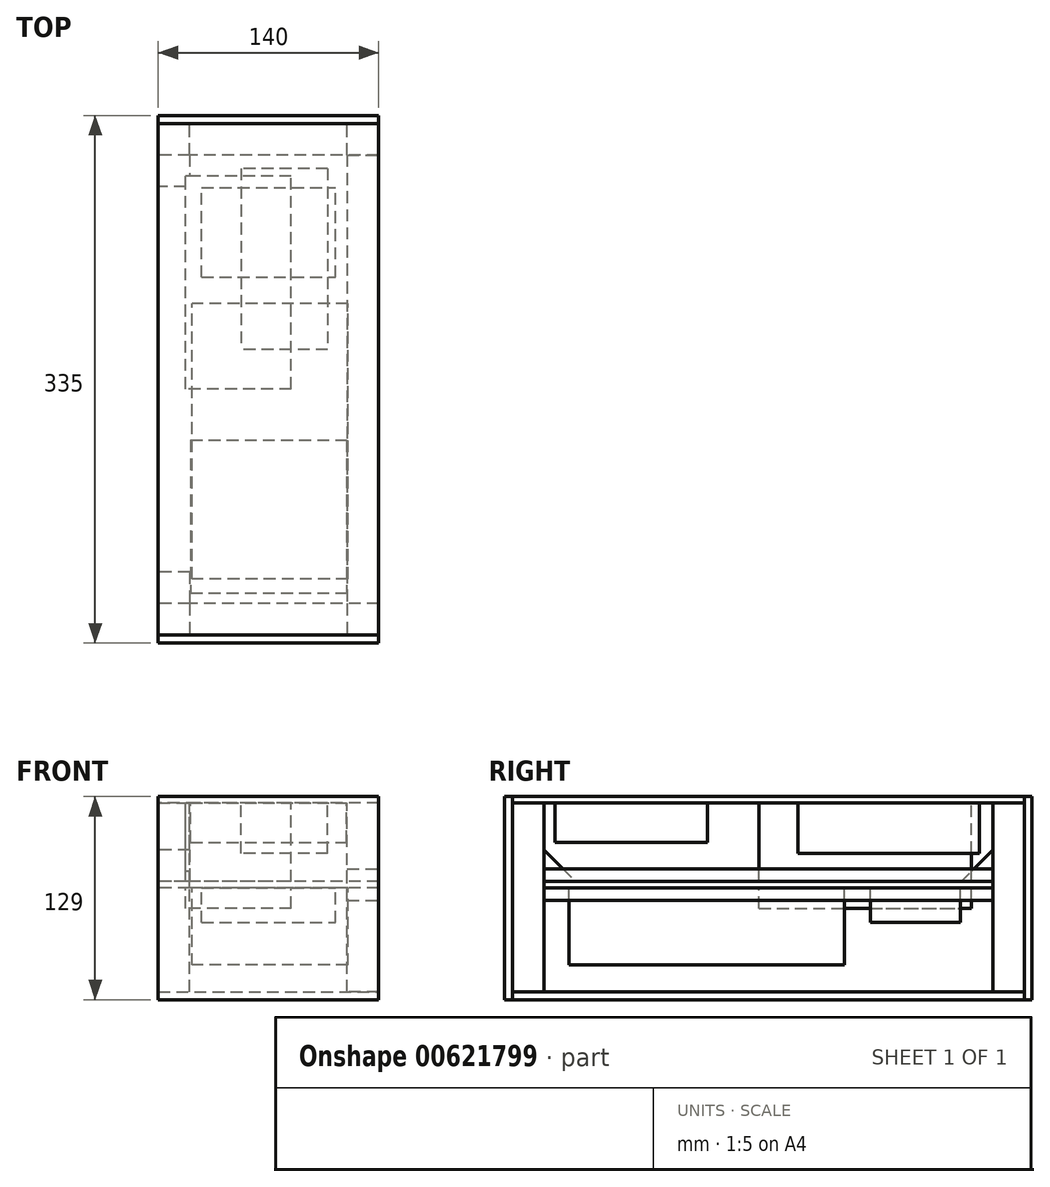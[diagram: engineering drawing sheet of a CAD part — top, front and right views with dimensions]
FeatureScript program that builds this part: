
annotation { "Feature Type Name" : "Feature", "Feature Type Description" : "" }
export const myFeature = defineFeature(function(context is Context, id is Id, definition is map)
    precondition{}
    {
        {
            var Q0;
            Q0=qCreatedBy(makeId("Top.planeOp"),FACE);
            var sketch = newSketch(context, id + "F0", { "sketchPlane" : qUnion([Q0])});
            skLineSegment(sketch, "E0.bottom", {"start": v(70, 142.5) * mm, "end": v(-70, 142.5) * mm, "construction": true});
            skLineSegment(sketch, "E0.top", {"start": v(70, -142.5) * mm, "end": v(-70, -142.5) * mm, "construction": true});
            skLineSegment(sketch, "E0.left", {"start": v(70, 142.5) * mm, "end": v(70, -142.5) * mm, "construction": true});
            skLineSegment(sketch, "E0.right", {"start": v(-70, 142.5) * mm, "end": v(-70, -142.5) * mm, "construction": true});
            skPoint(sketch, "E0.middle", {"position": v(0, 0) * mm});
            skLineSegment(sketch, "E1.bottom", {"start": v(70, -142.5) * mm, "end": v(50, -142.5) * mm});
            skLineSegment(sketch, "E1.top", {"start": v(70, -162.5) * mm, "end": v(50, -162.5) * mm});
            skLineSegment(sketch, "E1.left", {"start": v(70, -142.5) * mm, "end": v(70, -162.5) * mm});
            skLineSegment(sketch, "E1.right", {"start": v(50, -142.5) * mm, "end": v(50, -162.5) * mm});
            skLineSegment(sketch, "E2.bottom", {"start": v(-70, -142.5) * mm, "end": v(-50, -142.5) * mm});
            skLineSegment(sketch, "E2.top", {"start": v(-70, -162.5) * mm, "end": v(-50, -162.5) * mm});
            skLineSegment(sketch, "E2.left", {"start": v(-70, -142.5) * mm, "end": v(-70, -162.5) * mm});
            skLineSegment(sketch, "E2.right", {"start": v(-50, -142.5) * mm, "end": v(-50, -162.5) * mm});
            skLineSegment(sketch, "E3.bottom", {"start": v(-70, 142.5) * mm, "end": v(-50, 142.5) * mm});
            skLineSegment(sketch, "E3.top", {"start": v(-70, 162.5) * mm, "end": v(-50, 162.5) * mm});
            skLineSegment(sketch, "E3.left", {"start": v(-70, 142.5) * mm, "end": v(-70, 162.5) * mm});
            skLineSegment(sketch, "E3.right", {"start": v(-50, 142.5) * mm, "end": v(-50, 162.5) * mm});
            skLineSegment(sketch, "E4.bottom", {"start": v(70, 142.5) * mm, "end": v(50, 142.5) * mm});
            skLineSegment(sketch, "E4.top", {"start": v(70, 162.5) * mm, "end": v(50, 162.5) * mm});
            skLineSegment(sketch, "E4.left", {"start": v(70, 142.5) * mm, "end": v(70, 162.5) * mm});
            skLineSegment(sketch, "E4.right", {"start": v(50, 142.5) * mm, "end": v(50, 162.5) * mm});
            skSolve(sketch);
        }
        {
            var Q0;
            Q0=qCreatedBy(makeId("Top.planeOp"),FACE);
            var sketch = newSketch(context, id + "F1", { "sketchPlane" : qUnion([Q0])});
            skLineSegment(sketch, "E5.bottom", {"start": v(70, -162.5) * mm, "end": v(-70, -162.5) * mm});
            skLineSegment(sketch, "E5.top", {"start": v(70, 162.5) * mm, "end": v(-70, 162.5) * mm});
            skLineSegment(sketch, "E5.left", {"start": v(70, -162.5) * mm, "end": v(70, 162.5) * mm});
            skLineSegment(sketch, "E5.right", {"start": v(-70, -162.5) * mm, "end": v(-70, 162.5) * mm});
            skSolve(sketch);
        }
        {
            var Q0;
            Q0 = qSketchRegion(id + "F1", true);
            extrude(context, id + "F2", {"entities" : qUnion([Q0]), "depth" : 4 * mm, "offsetDistance" : 25 * mm});
        }
        {
            var Q0;
            Q0 = qSketchRegion(id + "F0", true);
            extrude(context, id + "F3", {"entities" : qUnion([Q0]), "oppositeDirection" : true, "depth" : 120 * mm, "offsetDistance" : 25 * mm});
        }
        {
            var Q0;
            Q0=qCreatedBy(makeId("Top.planeOp"),FACE);
            cPlane(context, id + "F4", {"entities" : qUnion([Q0]), "cplaneType" : CPlaneType.OFFSET, "offset" : 50 * mm, "oppositeDirection" : true, "width" : 150 * mm, "height" : 150 * mm});
        }
        {
            var Q0;
            Q0=qCreatedBy(id+"F4.planeOp",FACE);
            var sketch = newSketch(context, id + "F5", { "sketchPlane" : qUnion([Q0])});
            skLineSegment(sketch, "E6.bottom", {"start": v(50, -162.5) * mm, "end": v(-50, -162.5) * mm, "construction": true});
            skLineSegment(sketch, "E6.top", {"start": v(50, 162.5) * mm, "end": v(-50, 162.5) * mm, "construction": true});
            skLineSegment(sketch, "E6.left", {"start": v(70, -142.5) * mm, "end": v(70, 142.5) * mm});
            skLineSegment(sketch, "E6.right", {"start": v(-70, -142.5) * mm, "end": v(-70, 142.5) * mm});
            skLineSegment(sketch, "E7.0", {"start": v(70, -142.5) * mm, "end": v(50, -142.5) * mm});
            skLineSegment(sketch, "E7.1", {"start": v(50, -142.5) * mm, "end": v(50, -162.5) * mm, "construction": true});
            skLineSegment(sketch, "E7.2", {"start": v(-50, -142.5) * mm, "end": v(-50, -162.5) * mm, "construction": true});
            skLineSegment(sketch, "E7.3", {"start": v(-70, -142.5) * mm, "end": v(-50, -142.5) * mm});
            skLineSegment(sketch, "E7.4", {"start": v(-70, 142.5) * mm, "end": v(-50, 142.5) * mm});
            skLineSegment(sketch, "E7.5", {"start": v(-50, 142.5) * mm, "end": v(-50, 162.5) * mm, "construction": true});
            skLineSegment(sketch, "E7.6", {"start": v(50, 142.5) * mm, "end": v(50, 162.5) * mm, "construction": true});
            skLineSegment(sketch, "E7.7", {"start": v(70, 142.5) * mm, "end": v(50, 142.5) * mm});
            skLineSegment(sketch, "E8", {"start": v(50, -142.5) * mm, "end": v(-50, -142.5) * mm});
            skLineSegment(sketch, "E9", {"start": v(50, 142.5) * mm, "end": v(-50, 142.5) * mm});
            skSolve(sketch);
        }
        {
            var Q0;
            Q0 = qSketchRegion(id + "F5", true);
            extrude(context, id + "F6", {"entities" : qUnion([Q0]), "oppositeDirection" : true, "depth" : 4 * mm, "offsetDistance" : 25 * mm});
        }
        {
            var Q0;
            Q0=makeQuery(id+"F2.opExtrude","CAP_FACE",FACE,{"disambiguationData":[OSD([sQuery(id+"F1.wireOp",EDGE,"E5.bottom"),sQuery(id+"F1.wireOp",EDGE,"E5.top"),sQuery(id+"F1.wireOp",EDGE,"E5.left"),sQuery(id+"F1.wireOp",EDGE,"E5.right")])],"isStart":true});
            var sketch = newSketch(context, id + "F7", { "sketchPlane" : qUnion([Q0])});
            skLineSegment(sketch, "E10.bottom", {"start": v(37.67, -133.95) * mm, "end": v(-17.33, -133.95) * mm});
            skLineSegment(sketch, "E10.top", {"start": v(37.67, -18.95) * mm, "end": v(-17.33, -18.95) * mm});
            skLineSegment(sketch, "E10.left", {"start": v(37.67, -133.95) * mm, "end": v(37.67, -18.95) * mm});
            skLineSegment(sketch, "E10.right", {"start": v(-17.33, -133.95) * mm, "end": v(-17.33, -18.95) * mm});
            skPoint(sketch, "E10.middle", {"position": v(10.17, -76.45) * mm});
            skSolve(sketch);
        }
        {
            var Q0;
            Q0 = qSketchRegion(id + "F7", true);
            extrude(context, id + "F8", {"entities" : qUnion([Q0]), "depth" : 32 * mm, "offsetDistance" : 25 * mm});
        }
        {
            var Q0;
            Q0=makeQuery(id+"F6.opExtrude","CAP_FACE",FACE,{"disambiguationData":[OSD([sQuery(id+"F5.wireOp",EDGE,"E6.bottom"),sQuery(id+"F5.wireOp",EDGE,"E6.top"),sQuery(id+"F5.wireOp",EDGE,"E6.left"),sQuery(id+"F5.wireOp",EDGE,"E6.right"),sQuery(id+"F5.wireOp",EDGE,"E7.0"),sQuery(id+"F5.wireOp",EDGE,"E7.1"),sQuery(id+"F5.wireOp",EDGE,"E7.2"),sQuery(id+"F5.wireOp",EDGE,"E7.3"),sQuery(id+"F5.wireOp",EDGE,"E7.4"),sQuery(id+"F5.wireOp",EDGE,"E7.5"),sQuery(id+"F5.wireOp",EDGE,"E7.6"),sQuery(id+"F5.wireOp",EDGE,"E7.7")])],"isStart":false});
            var sketch = newSketch(context, id + "F9", { "sketchPlane" : qUnion([Q0])});
            skLineSegment(sketch, "E11.bottom", {"start": v(50.48, 126.75) * mm, "end": v(-48.52, 126.75) * mm});
            skLineSegment(sketch, "E11.top", {"start": v(50.48, -48.25) * mm, "end": v(-48.52, -48.25) * mm});
            skLineSegment(sketch, "E11.left", {"start": v(50.48, 126.75) * mm, "end": v(50.48, -48.25) * mm});
            skLineSegment(sketch, "E11.right", {"start": v(-48.52, 126.75) * mm, "end": v(-48.52, -48.25) * mm});
            skPoint(sketch, "E12.startSnap0", {"position": v(70, 0) * mm});
            skSolve(sketch);
        }
        {
            var Q0;
            Q0 = qSketchRegion(id + "F9", true);
            extrude(context, id + "F10", {"entities" : qUnion([Q0]), "depth" : 49 * mm, "offsetDistance" : 25 * mm});
        }
        {
            var Q0;
            Q0=qCreatedBy(id+"F4.planeOp",FACE);
            cPlane(context, id + "F11", {"entities" : qUnion([Q0]), "cplaneType" : CPlaneType.OFFSET, "offset" : 75 * mm, "oppositeDirection" : true, "width" : 150 * mm, "height" : 150 * mm});
        }
        {
            var Q0;
            Q0=makeQuery(id+"F2.opExtrude","CAP_FACE",FACE,{"disambiguationData":[OSD([sQuery(id+"F1.wireOp",EDGE,"E5.bottom"),sQuery(id+"F1.wireOp",EDGE,"E5.top"),sQuery(id+"F1.wireOp",EDGE,"E5.left"),sQuery(id+"F1.wireOp",EDGE,"E5.right")])],"isStart":true});
            var sketch = newSketch(context, id + "F12", { "sketchPlane" : qUnion([Q0])});
            skLineSegment(sketch, "E13.bottom", {"start": v(-49.5, 38.63) * mm, "end": v(49.5, 38.63) * mm});
            skLineSegment(sketch, "E13.top", {"start": v(-49.5, 135.63) * mm, "end": v(49.5, 135.63) * mm});
            skLineSegment(sketch, "E13.left", {"start": v(-49.5, 38.63) * mm, "end": v(-49.5, 135.63) * mm});
            skLineSegment(sketch, "E13.right", {"start": v(49.5, 38.63) * mm, "end": v(49.5, 135.63) * mm});
            skPoint(sketch, "E13.middle", {"position": v(0, 87.13) * mm});
            skSolve(sketch);
        }
        {
            var Q0;
            Q0 = qSketchRegion(id + "F12", true);
            var Q1;
            Q1=sQuery(id+"F12.wireOp",EDGE,"E13.left");
            extrude(context, id + "F13", {"entities" : qUnion([Q0]), "surfaceEntities" : qUnion([Q1]), "depth" : 25 * mm, "offsetDistance" : 25 * mm});
        }
        {
            var Q0;
            Q0=makeQuery(id+"F6.opExtrude","CAP_FACE",FACE,{"disambiguationData":[OSD([sQuery(id+"F5.wireOp",EDGE,"E6.bottom"),sQuery(id+"F5.wireOp",EDGE,"E6.top"),sQuery(id+"F5.wireOp",EDGE,"E6.left"),sQuery(id+"F5.wireOp",EDGE,"E6.right"),sQuery(id+"F5.wireOp",EDGE,"E7.0"),sQuery(id+"F5.wireOp",EDGE,"E7.1"),sQuery(id+"F5.wireOp",EDGE,"E7.2"),sQuery(id+"F5.wireOp",EDGE,"E7.3"),sQuery(id+"F5.wireOp",EDGE,"E7.4"),sQuery(id+"F5.wireOp",EDGE,"E7.5"),sQuery(id+"F5.wireOp",EDGE,"E7.6"),sQuery(id+"F5.wireOp",EDGE,"E7.7")])],"isStart":false});
            var sketch = newSketch(context, id + "F14", { "sketchPlane" : qUnion([Q0])});
            skLineSegment(sketch, "E14.bottom", {"start": v(-42.5, -64.85) * mm, "end": v(42.5, -64.85) * mm});
            skLineSegment(sketch, "E14.top", {"start": v(-42.5, -121.85) * mm, "end": v(42.5, -121.85) * mm});
            skLineSegment(sketch, "E14.left", {"start": v(-42.5, -64.85) * mm, "end": v(-42.5, -121.85) * mm});
            skLineSegment(sketch, "E14.right", {"start": v(42.5, -64.85) * mm, "end": v(42.5, -121.85) * mm});
            skPoint(sketch, "E14.middle", {"position": v(0, -93.35) * mm});
            skSolve(sketch);
        }
        {
            var Q0;
            Q0 = qSketchRegion(id + "F14", true);
            extrude(context, id + "F15", {"entities" : qUnion([Q0]), "depth" : 22 * mm, "offsetDistance" : 25 * mm});
        }
        {
            var Q0;
            Q0=makeQuery(id+"F3.opExtrude","CAP_FACE",FACE,{"disambiguationData":[OSD([sQuery(id+"F0.wireOp",EDGE,"E4.bottom"),sQuery(id+"F0.wireOp",EDGE,"E4.top"),sQuery(id+"F0.wireOp",EDGE,"E4.left"),sQuery(id+"F0.wireOp",EDGE,"E4.right")])],"isStart":false});
            var sketch = newSketch(context, id + "F16", { "sketchPlane" : qUnion([Q0])});
            skLineSegment(sketch, "E15.bottom", {"start": v(-70, -162.5) * mm, "end": v(70, -162.5) * mm});
            skLineSegment(sketch, "E15.top", {"start": v(-70, 162.5) * mm, "end": v(70, 162.5) * mm});
            skLineSegment(sketch, "E15.left", {"start": v(-70, -162.5) * mm, "end": v(-70, 162.5) * mm});
            skLineSegment(sketch, "E15.right", {"start": v(70, -162.5) * mm, "end": v(70, 162.5) * mm});
            skSolve(sketch);
        }
        {
            var Q0;
            Q0 = qSketchRegion(id + "F16", true);
            extrude(context, id + "F17", {"entities" : qUnion([Q0]), "depth" : 5 * mm, "offsetDistance" : 25 * mm});
        }
        {
            var Q0;
            Q0=makeQuery(id+"F3.opExtrude","SWEPT_FACE",FACE,{"disambiguationData":[OSD([sQuery(id+"F0.wireOp",EDGE,"E3.left")])]});
            var sketch = newSketch(context, id + "F18", { "sketchPlane" : qUnion([Q0])});
            skLineSegment(sketch, "E16", {"start": v(-122.5, -50) * mm, "end": v(-142.5, -50) * mm});
            skLineSegment(sketch, "E17", {"start": v(-142.5, -50) * mm, "end": v(-142.5, -30) * mm});
            skLineSegment(sketch, "E18", {"start": v(-142.5, -30) * mm, "end": v(-122.5, -50) * mm});
            skLineSegment(sketch, "E19", {"start": v(142.5, -50) * mm, "end": v(142.5, -30) * mm});
            skLineSegment(sketch, "E20", {"start": v(142.5, -30) * mm, "end": v(122.5, -50) * mm});
            skLineSegment(sketch, "E21", {"start": v(122.5, -50) * mm, "end": v(142.5, -50) * mm});
            skSolve(sketch);
        }
        {
            var Q0;
            Q0=makeQuery(id+"Fl6m5WLlSnuW4oQ_12.boolean.opBoolean","MERGE",FACE,{"derivedFrom":[makeQuery(id+"F3.opExtrude","SWEPT_FACE",FACE,{"disambiguationData":[OSD([sQuery(id+"F0.wireOp",EDGE,"E4.left")])]}),makeQuery(id+"Fl6m5WLlSnuW4oQ_12.opExtrude","CAP_FACE",FACE,{"disambiguationData":[OSD([sQuery(id+"FpnPx7z1yVd2ZUk_12.wireOp",EDGE,"db6a5ccb-9548-4f94-9b98-553bb2cdde76.0"),sQuery(id+"FpnPx7z1yVd2ZUk_12.wireOp",EDGE,"db6a5ccb-9548-4f94-9b98-553bb2cdde76.1"),sQuery(id+"FpnPx7z1yVd2ZUk_12.wireOp",EDGE,"db6a5ccb-9548-4f94-9b98-553bb2cdde76.2")])],"isStart":true}),makeQuery(id+"Fl6m5WLlSnuW4oQ_12.opExtrude","CAP_FACE",FACE,{"disambiguationData":[OSD([sQuery(id+"FpnPx7z1yVd2ZUk_12.wireOp",EDGE,"db6a5ccb-9548-4f94-9b98-553bb2cdde76.3"),sQuery(id+"FpnPx7z1yVd2ZUk_12.wireOp",EDGE,"db6a5ccb-9548-4f94-9b98-553bb2cdde76.4"),sQuery(id+"FpnPx7z1yVd2ZUk_12.wireOp",EDGE,"db6a5ccb-9548-4f94-9b98-553bb2cdde76.5")])],"isStart":true})]});
            var sketch = newSketch(context, id + "F19", { "sketchPlane" : qUnion([Q0])});
            skLineSegment(sketch, "E22.bottom", {"start": v(162.5, -125) * mm, "end": v(-162.5, -125) * mm});
            skLineSegment(sketch, "E22.top", {"start": v(162.5, 4) * mm, "end": v(-162.5, 4) * mm});
            skLineSegment(sketch, "E22.left", {"start": v(162.5, -125) * mm, "end": v(162.5, 4) * mm});
            skLineSegment(sketch, "E22.right", {"start": v(-162.5, -125) * mm, "end": v(-162.5, 4) * mm});
            skSolve(sketch);
        }
        {
            var Q0;
            Q0=makeQuery(id+"F3.opExtrude","SWEPT_FACE",FACE,{"disambiguationData":[OSD([sQuery(id+"F0.wireOp",EDGE,"E3.top")])]});
            var sketch = newSketch(context, id + "F20", { "sketchPlane" : qUnion([Q0])});
            skLineSegment(sketch, "E23.bottom", {"start": v(70, -125) * mm, "end": v(-70, -125) * mm});
            skLineSegment(sketch, "E23.top", {"start": v(70, 4) * mm, "end": v(-70, 4) * mm});
            skLineSegment(sketch, "E23.left", {"start": v(70, -125) * mm, "end": v(70, 4) * mm});
            skLineSegment(sketch, "E23.right", {"start": v(-70, -125) * mm, "end": v(-70, 4) * mm});
            skSolve(sketch);
        }
        {
            var Q0;
            Q0 = qSketchRegion(id + "F20", true);
            extrude(context, id + "F21", {"entities" : qUnion([Q0]), "depth" : 5 * mm, "offsetDistance" : 25 * mm});
        }
        {
            var Q0;
            Q0=makeQuery(id+"F3.opExtrude","SWEPT_FACE",FACE,{"disambiguationData":[OSD([sQuery(id+"F0.wireOp",EDGE,"E2.top")])]});
            var sketch = newSketch(context, id + "F22", { "sketchPlane" : qUnion([Q0])});
            skLineSegment(sketch, "E24.bottom", {"start": v(-70, -125) * mm, "end": v(70, -125) * mm});
            skLineSegment(sketch, "E24.top", {"start": v(-70, 4) * mm, "end": v(70, 4) * mm});
            skLineSegment(sketch, "E24.left", {"start": v(-70, -125) * mm, "end": v(-70, 4) * mm});
            skLineSegment(sketch, "E24.right", {"start": v(70, -125) * mm, "end": v(70, 4) * mm});
            skSolve(sketch);
        }
        {
            var Q0;
            Q0 = qSketchRegion(id + "F22", true);
            extrude(context, id + "F23", {"entities" : qUnion([Q0]), "depth" : 5 * mm, "offsetDistance" : 25 * mm});
        }
        {
            var Q0;
            Q0=makeQuery(id+"F2.opExtrude","CAP_FACE",FACE,{"disambiguationData":[OSD([sQuery(id+"F1.wireOp",EDGE,"E5.bottom"),sQuery(id+"F1.wireOp",EDGE,"E5.top"),sQuery(id+"F1.wireOp",EDGE,"E5.left"),sQuery(id+"F1.wireOp",EDGE,"E5.right")])],"isStart":true});
            var sketch = newSketch(context, id + "F24", { "sketchPlane" : qUnion([Q0])});
            skLineSegment(sketch, "E25.bottom", {"start": v(14.42, 6) * mm, "end": v(-52.58, 6) * mm});
            skLineSegment(sketch, "E25.top", {"start": v(14.42, -129) * mm, "end": v(-52.58, -129) * mm});
            skLineSegment(sketch, "E25.left", {"start": v(14.42, 6) * mm, "end": v(14.42, -129) * mm});
            skLineSegment(sketch, "E25.right", {"start": v(-52.58, 6) * mm, "end": v(-52.58, -129) * mm});
            skSolve(sketch);
        }
        {
            var Q0;
            Q0 = qSketchRegion(id + "F24", true);
            extrude(context, id + "F25", {"entities" : qUnion([Q0]), "depth" : 67 * mm, "offsetDistance" : 25 * mm});
        }
        {
            var Q0;
            Q0 = qSketchRegion(id + "F18", true);
            extrude(context, id + "F26", {"entities" : qUnion([Q0]), "operationType" : NewBodyOperationType.ADD, "oppositeDirection" : true, "depth" : 20 * mm, "offsetDistance" : 25 * mm});
        }
        {
            var Q0;
            Q0=makeQuery(id+"F3.opExtrude","SWEPT_FACE",FACE,{"disambiguationData":[OSD([sQuery(id+"F0.wireOp",EDGE,"E1.bottom")])]});
            var sketch = newSketch(context, id + "F27", { "sketchPlane" : qUnion([Q0])});
            skLineSegment(sketch, "E26.bottom", {"start": v(-50, -62) * mm, "end": v(-70, -62) * mm});
            skLineSegment(sketch, "E26.top", {"start": v(-50, -42) * mm, "end": v(-70, -42) * mm});
            skLineSegment(sketch, "E26.left", {"start": v(-50, -62) * mm, "end": v(-50, -42) * mm});
            skLineSegment(sketch, "E26.right", {"start": v(-70, -62) * mm, "end": v(-70, -42) * mm});
            skPoint(sketch, "E27", {"position": v(-70, -52) * mm});
            skSolve(sketch);
        }
        {
            var Q0;
            Q0 = qSketchRegion(id + "F27", true);
            var Q1;
            Q1=makeQuery(id+"F3.opExtrude","SWEPT_FACE",FACE,{"disambiguationData":[OSD([sQuery(id+"F0.wireOp",EDGE,"E4.bottom")])]});
            extrude(context, id + "F28", {"entities" : qUnion([Q0]), "endBound" : BoundingType.UP_TO_SURFACE, "depth" : 25 * mm, "endBoundEntityFace" : qUnion([Q1]), "offsetDistance" : 25 * mm});
        }
    });
